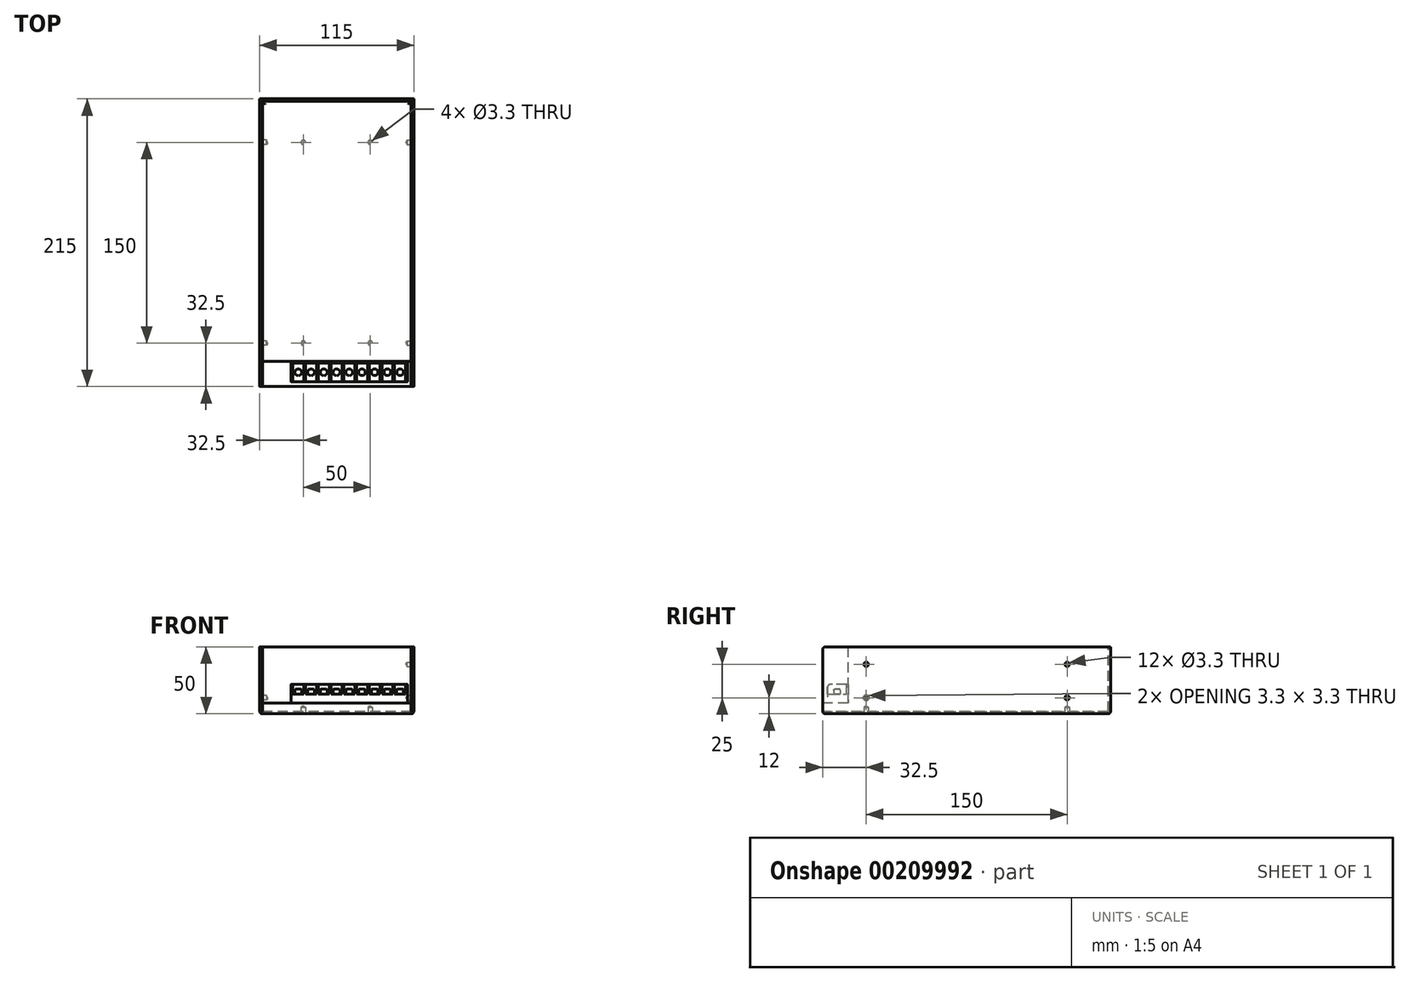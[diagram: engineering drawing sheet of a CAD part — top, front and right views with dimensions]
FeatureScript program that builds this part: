
annotation { "Feature Type Name" : "Feature", "Feature Type Description" : "" }
export const myFeature = defineFeature(function(context is Context, id is Id, definition is map)
    precondition{}
    {
        {
            var Q0;
            Q0=qCreatedBy(makeId("Front.planeOp"),FACE);
            var sketch = newSketch(context, id + "F0", { "sketchPlane" : qUnion([Q0])});
            skLineSegment(sketch, "E0.bottom", {"start": v(-57.5, 25) * mm, "end": v(0, 25) * mm});
            skLineSegment(sketch, "E0.top", {"start": v(-57.5, -25) * mm, "end": v(0, -25) * mm});
            skLineSegment(sketch, "E0.left", {"start": v(-57.5, 25) * mm, "end": v(-57.5, -25) * mm});
            skLineSegment(sketch, "E0.right", {"start": v(0, 25) * mm, "end": v(0, -25) * mm});
            skLineSegment(sketch, "E1", {"start": v(0, 0) * mm, "end": v(0, 48.13) * mm, "construction": true});
            skLineSegment(sketch, "E2", {"start": v(0, 0) * mm, "end": v(-98.9, 0) * mm, "construction": true});
            skPoint(sketch, "E2.endSnap0", {"position": v(0, 0) * mm});
            skSolve(sketch);
        }
        {
            var Q0;
            Q0=makeQuery(id+"F0.imprint","IMPRINT",FACE,{"disambiguationData":[TD([[makeQuery(id+"F0.imprint","IMPRINT",EDGE,{"derivedFrom":sQuery(id+"F0.wireOp",EDGE,"E0.bottom")}),-1.0]])]});
            extrude(context, id + "F1", {"entities" : qUnion([Q0]), "endBound" : BoundingType.SYMMETRIC, "depth" : 215 * mm});
        }
        {
            var Q0;
            Q0=makeQuery(id+"F1.opExtrude","SWEPT_FACE",FACE,{"disambiguationData":[OSD([sQuery(id+"F0.wireOp",EDGE,"E0.bottom")])]});
            var sketch = newSketch(context, id + "F2", { "sketchPlane" : qUnion([Q0])});
            skLineSegment(sketch, "E3.bottom", {"start": v(0, -107.5) * mm, "end": v(-55.8, -107.5) * mm});
            skLineSegment(sketch, "E3.top", {"start": v(0, -88.5) * mm, "end": v(-55.8, -88.5) * mm});
            skLineSegment(sketch, "E3.left", {"start": v(0, -107.5) * mm, "end": v(0, -88.5) * mm});
            skLineSegment(sketch, "E3.right", {"start": v(-55.8, -107.5) * mm, "end": v(-55.8, -88.5) * mm});
            skSolve(sketch);
        }
        {
            var Q0;
            Q0=makeQuery(id+"F2.imprint","IMPRINT",FACE,{"disambiguationData":[TD([[makeQuery(id+"F2.imprint","IMPRINT",EDGE,{"derivedFrom":sQuery(id+"F2.wireOp",EDGE,"E3.bottom")}),1.0]])]});
            extrude(context, id + "F3", {"entities" : qUnion([Q0]), "operationType" : NewBodyOperationType.REMOVE, "oppositeDirection" : true, "depth" : 42 * mm});
        }
        {
            var Q0;
            Q0=makeQuery(id+"F1.opExtrude","SWEPT_FACE",FACE,{"disambiguationData":[OSD([sQuery(id+"F0.wireOp",EDGE,"E0.bottom")])]});
            var sketch = newSketch(context, id + "F4", { "sketchPlane" : qUnion([Q0])});
            skLineSegment(sketch, "E4", {"start": v(-55.8, -107.5) * mm, "end": v(-55.8, 107.5) * mm});
            skLineSegment(sketch, "E5", {"start": v(-55.8, 107.5) * mm, "end": v(-55.5, 107.5) * mm});
            skLineSegment(sketch, "E6", {"start": v(-55.5, 107.5) * mm, "end": v(-55.5, 105.8) * mm});
            skLineSegment(sketch, "E7", {"start": v(-55.5, 105.8) * mm, "end": v(0, 105.8) * mm});
            skLineSegment(sketch, "E8", {"start": v(0, 105.8) * mm, "end": v(0, 105.5) * mm});
            skLineSegment(sketch, "E9", {"start": v(0, 105.5) * mm, "end": v(-55.5, 105.5) * mm});
            skLineSegment(sketch, "E10", {"start": v(-55.5, 105.5) * mm, "end": v(-55.5, -107.5) * mm});
            skLineSegment(sketch, "E11", {"start": v(-55.5, -107.5) * mm, "end": v(-55.8, -107.5) * mm});
            skSolve(sketch);
        }
        {
            var Q0;
            {var subQ1=sQuery(id+"F4.wireOp",EDGE,"E5");Q0=makeQuery(id+"F4.imprint","IMPRINT",FACE,{"disambiguationData":[TD([[makeQuery(id+"F4.imprint","IMPRINT",EDGE,{"derivedFrom":subQ1}),-1.0]])]});}
            var Q1;
            {var subQ0=sQuery(id+"F4.wireOp",EDGE,"E11");Q1=makeQuery(id+"F4.imprint","IMPRINT",FACE,{"disambiguationData":[TD([[makeQuery(id+"F4.imprint","IMPRINT",EDGE,{"derivedFrom":subQ0}),-1.0]])]});}
            extrude(context, id + "F5", {"entities" : qUnion([Q0, Q1]), "operationType" : NewBodyOperationType.REMOVE, "oppositeDirection" : true, "depth" : 48.3 * mm});
        }
        {
            var Q0;
            Q0=makeQuery(id+"F3.boolean.opBoolean","COPY",EDGE,{"derivedFrom":makeQuery(id+"F3.opExtrude","CAP_EDGE",EDGE,{"disambiguationData":[OSD([sQuery(id+"F2.wireOp",EDGE,"E3.top")])],"isStart":true})});
            var Q1;
            Q1=makeQuery(id+"F1.opExtrude","CAP_EDGE",EDGE,{"disambiguationData":[OSD([sQuery(id+"F0.wireOp",EDGE,"E0.top")])],"isStart":false});
            var Q2;
            Q2=makeQuery(id+"F1.opExtrude","SWEPT_EDGE",EDGE,{"disambiguationData":[OSD([sQuery(id+"F0.wireOp",EDGE,"E0.top"),sQuery(id+"F0.wireOp",EDGE,"E0.left")])]});
            var Q3;
            Q3=makeQuery(id+"F1.opExtrude","CAP_EDGE",EDGE,{"disambiguationData":[OSD([sQuery(id+"F0.wireOp",EDGE,"E0.top")])],"isStart":true});
            var Q4;
            Q4=makeQuery(id+"F1.opExtrude","CAP_EDGE",EDGE,{"disambiguationData":[OSD([sQuery(id+"F0.wireOp",EDGE,"E0.bottom")])],"isStart":false});
            var Q5;
            {var subQ0=sQuery(id+"F0.wireOp",EDGE,"E0.bottom");var subQ1=sQuery(id+"F0.wireOp",EDGE,"E0.left");Q5=makeQuery(id+"F5.boolean.opBoolean","SPLIT",EDGE,{"disambiguationData":[TD([makeQuery(id+"F1.opExtrude","SWEPT_FACE",FACE,{"disambiguationData":[OSD([subQ1])]})])],"derivedFrom":makeQuery(id+"F1.opExtrude","CAP_EDGE",EDGE,{"disambiguationData":[OSD([subQ0])],"isStart":true})});}
            var Q6;
            Q6=makeQuery(id+"F5.boolean.opBoolean","COPY",EDGE,{"derivedFrom":makeQuery(id+"F5.opExtrude","CAP_EDGE",EDGE,{"disambiguationData":[OSD([sQuery(id+"F4.wireOp",EDGE,"E6")])],"isStart":true})});
            var Q7;
            Q7=makeQuery(id+"F5.boolean.opBoolean","COPY",EDGE,{"derivedFrom":makeQuery(id+"F5.opExtrude","CAP_EDGE",EDGE,{"disambiguationData":[OSD([sQuery(id+"F4.wireOp",EDGE,"E9")])],"isStart":true})});
            var Q8;
            Q8=makeQuery(id+"F5.boolean.opBoolean","COPY",EDGE,{"derivedFrom":makeQuery(id+"F5.opExtrude","CAP_EDGE",EDGE,{"disambiguationData":[OSD([sQuery(id+"F4.wireOp",EDGE,"E10")])],"isStart":true})});
            fillet(context, id + "F6", {"entities" : qUnion([Q0, Q1, Q2, Q3, Q4, Q5, Q6, Q7, Q8]), "radius" : 2 * mm, "tangentPropagation" : true, "allowEdgeOverflow" : false});
        }
        {
            var Q0;
            Q0=makeQuery(id+"F1.opExtrude","SWEPT_BODY",BODY,{"disambiguationData":[OSD([sQuery(id+"F0.wireOp",EDGE,"E0.bottom"),sQuery(id+"F0.wireOp",EDGE,"E0.top"),sQuery(id+"F0.wireOp",EDGE,"E0.left"),sQuery(id+"F0.wireOp",EDGE,"E0.right")])]});
            var Q1;
            Q1=qCreatedBy(makeId("Right.planeOp"),FACE);
            mirror(context, id + "F7", {"operationType" : NewBodyOperationType.ADD, "entities" : qUnion([Q0]), "mirrorPlane" : qUnion([Q1])});
        }
        {
            var Q0;
            {var subQ0=makeQuery(id+"F3.boolean.opBoolean","COPY",FACE,{"derivedFrom":makeQuery(id+"F3.opExtrude","CAP_FACE",FACE,{"disambiguationData":[OSD([sQuery(id+"F2.wireOp",EDGE,"E3.bottom"),sQuery(id+"F2.wireOp",EDGE,"E3.top"),sQuery(id+"F2.wireOp",EDGE,"E3.left"),sQuery(id+"F2.wireOp",EDGE,"E3.right")])],"isStart":false})});Q0=makeQuery(id+"F7.boolean.opBoolean","MERGE",FACE,{"derivedFrom":[subQ0,makeQuery(id+"F7.opPattern","COPY",FACE,{"derivedFrom":subQ0,"instanceName":"1"})]});}
            var sketch = newSketch(context, id + "F8", { "sketchPlane" : qUnion([Q0])});
            skLineSegment(sketch, "E12.bottom", {"start": v(-34.2, -88.5) * mm, "end": v(52.8, -88.5) * mm});
            skLineSegment(sketch, "E12.top", {"start": v(-34.2, -103.8) * mm, "end": v(52.8, -103.8) * mm});
            skLineSegment(sketch, "E12.left", {"start": v(-34.2, -88.5) * mm, "end": v(-34.2, -103.8) * mm});
            skLineSegment(sketch, "E12.right", {"start": v(52.8, -88.5) * mm, "end": v(52.8, -103.8) * mm});
            skSolve(sketch);
        }
        {
            var Q0;
            Q0=makeQuery(id+"F8.imprint","IMPRINT",FACE,{"disambiguationData":[TD([[makeQuery(id+"F8.imprint","IMPRINT",EDGE,{"derivedFrom":sQuery(id+"F8.wireOp",EDGE,"E12.bottom")}),1.0]])]});
            extrude(context, id + "F9", {"entities" : qUnion([Q0]), "depth" : 14 * mm});
        }
        {
            var Q0;
            Q0=makeQuery(id+"F9.opExtrude","CAP_FACE",FACE,{"disambiguationData":[OSD([sQuery(id+"F8.wireOp",EDGE,"E12.bottom"),sQuery(id+"F8.wireOp",EDGE,"E12.top"),sQuery(id+"F8.wireOp",EDGE,"E12.left"),sQuery(id+"F8.wireOp",EDGE,"E12.right")])],"isStart":false});
            var sketch = newSketch(context, id + "F10", { "sketchPlane" : qUnion([Q0])});
            skLineSegment(sketch, "E13", {"start": v(-32.8, -103.8) * mm, "end": v(-32.8, -89.8) * mm});
            skLineSegment(sketch, "E14", {"start": v(-32.8, -89.8) * mm, "end": v(-24.6, -89.8) * mm});
            skLineSegment(sketch, "E15", {"start": v(-24.6, -89.8) * mm, "end": v(-24.6, -103.8) * mm});
            skLineSegment(sketch, "E16", {"start": v(-24.6, -103.8) * mm, "end": v(-32.8, -103.8) * mm});
            skLineSegment(sketch, "E17.1.0.0", {"start": v(-23.3, -103.8) * mm, "end": v(-23.3, -89.8) * mm});
            skLineSegment(sketch, "E17.1.0.1", {"start": v(-15.1, -103.8) * mm, "end": v(-23.3, -103.8) * mm});
            skLineSegment(sketch, "E17.1.0.2", {"start": v(-15.1, -89.8) * mm, "end": v(-15.1, -103.8) * mm});
            skLineSegment(sketch, "E17.1.0.3", {"start": v(-23.3, -89.8) * mm, "end": v(-15.1, -89.8) * mm});
            skLineSegment(sketch, "E17.2.0.0", {"start": v(-13.8, -103.8) * mm, "end": v(-13.8, -89.8) * mm});
            skLineSegment(sketch, "E17.2.0.1", {"start": v(-5.6, -103.8) * mm, "end": v(-13.8, -103.8) * mm});
            skLineSegment(sketch, "E17.2.0.2", {"start": v(-5.6, -89.8) * mm, "end": v(-5.6, -103.8) * mm});
            skLineSegment(sketch, "E17.2.0.3", {"start": v(-13.8, -89.8) * mm, "end": v(-5.6, -89.8) * mm});
            skLineSegment(sketch, "E17.3.0.0", {"start": v(-4.3, -103.8) * mm, "end": v(-4.3, -89.8) * mm});
            skLineSegment(sketch, "E17.3.0.1", {"start": v(3.9, -103.8) * mm, "end": v(-4.3, -103.8) * mm});
            skLineSegment(sketch, "E17.3.0.2", {"start": v(3.9, -89.8) * mm, "end": v(3.9, -103.8) * mm});
            skLineSegment(sketch, "E17.3.0.3", {"start": v(-4.3, -89.8) * mm, "end": v(3.9, -89.8) * mm});
            skLineSegment(sketch, "E17.4.0.0", {"start": v(5.2, -103.8) * mm, "end": v(5.2, -89.8) * mm});
            skLineSegment(sketch, "E17.4.0.1", {"start": v(13.4, -103.8) * mm, "end": v(5.2, -103.8) * mm});
            skLineSegment(sketch, "E17.4.0.2", {"start": v(13.4, -89.8) * mm, "end": v(13.4, -103.8) * mm});
            skLineSegment(sketch, "E17.4.0.3", {"start": v(5.2, -89.8) * mm, "end": v(13.4, -89.8) * mm});
            skLineSegment(sketch, "E17.5.0.0", {"start": v(14.7, -103.8) * mm, "end": v(14.7, -89.8) * mm});
            skLineSegment(sketch, "E17.5.0.1", {"start": v(22.9, -103.8) * mm, "end": v(14.7, -103.8) * mm});
            skLineSegment(sketch, "E17.5.0.2", {"start": v(22.9, -89.8) * mm, "end": v(22.9, -103.8) * mm});
            skLineSegment(sketch, "E17.5.0.3", {"start": v(14.7, -89.8) * mm, "end": v(22.9, -89.8) * mm});
            skLineSegment(sketch, "E17.6.0.0", {"start": v(24.2, -103.8) * mm, "end": v(24.2, -89.8) * mm});
            skLineSegment(sketch, "E17.6.0.1", {"start": v(32.4, -103.8) * mm, "end": v(24.2, -103.8) * mm});
            skLineSegment(sketch, "E17.6.0.2", {"start": v(32.4, -89.8) * mm, "end": v(32.4, -103.8) * mm});
            skLineSegment(sketch, "E17.6.0.3", {"start": v(24.2, -89.8) * mm, "end": v(32.4, -89.8) * mm});
            skLineSegment(sketch, "E17.7.0.0", {"start": v(33.7, -103.8) * mm, "end": v(33.7, -89.8) * mm});
            skLineSegment(sketch, "E17.7.0.1", {"start": v(41.9, -103.8) * mm, "end": v(33.7, -103.8) * mm});
            skLineSegment(sketch, "E17.7.0.2", {"start": v(41.9, -89.8) * mm, "end": v(41.9, -103.8) * mm});
            skLineSegment(sketch, "E17.7.0.3", {"start": v(33.7, -89.8) * mm, "end": v(41.9, -89.8) * mm});
            skLineSegment(sketch, "E17.8.0.0", {"start": v(43.2, -103.8) * mm, "end": v(43.2, -89.8) * mm});
            skLineSegment(sketch, "E17.8.0.1", {"start": v(51.4, -103.8) * mm, "end": v(43.2, -103.8) * mm});
            skLineSegment(sketch, "E17.8.0.2", {"start": v(51.4, -89.8) * mm, "end": v(51.4, -103.8) * mm});
            skLineSegment(sketch, "E17.8.0.3", {"start": v(43.2, -89.8) * mm, "end": v(51.4, -89.8) * mm});
            skLineSegment(sketch, "E17.direction1", {"start": v(-32.8, -103.8) * mm, "end": v(-23.3, -103.8) * mm, "construction": true});
            skSolve(sketch);
        }
        {
            var Q0;
            Q0=makeQuery(id+"F10.imprint","IMPRINT",FACE,{"disambiguationData":[TD([[makeQuery(id+"F10.imprint","IMPRINT",EDGE,{"derivedFrom":sQuery(id+"F10.wireOp",EDGE,"E13")}),-1.0]])]});
            var Q1;
            Q1=makeQuery(id+"F10.imprint","IMPRINT",FACE,{"disambiguationData":[TD([[makeQuery(id+"F10.imprint","IMPRINT",EDGE,{"derivedFrom":sQuery(id+"F10.wireOp",EDGE,"E17.1.0.0")}),-1.0]])]});
            var Q2;
            Q2=makeQuery(id+"F10.imprint","IMPRINT",FACE,{"disambiguationData":[TD([[makeQuery(id+"F10.imprint","IMPRINT",EDGE,{"derivedFrom":sQuery(id+"F10.wireOp",EDGE,"E17.2.0.0")}),-1.0]])]});
            var Q3;
            Q3=makeQuery(id+"F10.imprint","IMPRINT",FACE,{"disambiguationData":[TD([[makeQuery(id+"F10.imprint","IMPRINT",EDGE,{"derivedFrom":sQuery(id+"F10.wireOp",EDGE,"E17.3.0.0")}),-1.0]])]});
            var Q4;
            Q4=makeQuery(id+"F10.imprint","IMPRINT",FACE,{"disambiguationData":[TD([[makeQuery(id+"F10.imprint","IMPRINT",EDGE,{"derivedFrom":sQuery(id+"F10.wireOp",EDGE,"E17.4.0.0")}),-1.0]])]});
            var Q5;
            Q5=makeQuery(id+"F10.imprint","IMPRINT",FACE,{"disambiguationData":[TD([[makeQuery(id+"F10.imprint","IMPRINT",EDGE,{"derivedFrom":sQuery(id+"F10.wireOp",EDGE,"E17.5.0.0")}),-1.0]])]});
            var Q6;
            Q6=makeQuery(id+"F10.imprint","IMPRINT",FACE,{"disambiguationData":[TD([[makeQuery(id+"F10.imprint","IMPRINT",EDGE,{"derivedFrom":sQuery(id+"F10.wireOp",EDGE,"E17.6.0.0")}),-1.0]])]});
            var Q7;
            Q7=makeQuery(id+"F10.imprint","IMPRINT",FACE,{"disambiguationData":[TD([[makeQuery(id+"F10.imprint","IMPRINT",EDGE,{"derivedFrom":sQuery(id+"F10.wireOp",EDGE,"E17.7.0.0")}),-1.0]])]});
            var Q8;
            Q8=makeQuery(id+"F10.imprint","IMPRINT",FACE,{"disambiguationData":[TD([[makeQuery(id+"F10.imprint","IMPRINT",EDGE,{"derivedFrom":sQuery(id+"F10.wireOp",EDGE,"E17.8.0.0")}),-1.0]])]});
            extrude(context, id + "F11", {"entities" : qUnion([Q0, Q1, Q2, Q3, Q4, Q5, Q6, Q7, Q8]), "operationType" : NewBodyOperationType.REMOVE, "oppositeDirection" : true, "depth" : 7.4 * mm});
        }
        {
            var Q0;
            {var subQ0=sQuery(id+"F8.wireOp",EDGE,"E12.left");var subQ1=sQuery(id+"F8.wireOp",EDGE,"E12.top");Q0=makeQuery(id+"F11.boolean.opBoolean","SPLIT",EDGE,{"disambiguationData":[TD([makeQuery(id+"F9.opExtrude","SWEPT_FACE",FACE,{"disambiguationData":[OSD([subQ0])]})])],"derivedFrom":makeQuery(id+"F9.opExtrude","CAP_EDGE",EDGE,{"disambiguationData":[OSD([subQ1])],"isStart":false})});}
            var Q1;
            {var subQ0=sQuery(id+"F8.wireOp",EDGE,"E12.top");Q1=makeQuery(id+"F11.boolean.opBoolean","SPLIT",EDGE,{"disambiguationData":[TD([makeQuery(id+"F11.opExtrude","SWEPT_FACE",FACE,{"disambiguationData":[OSD([sQuery(id+"F10.wireOp",EDGE,"E15")])]})])],"derivedFrom":makeQuery(id+"F9.opExtrude","CAP_EDGE",EDGE,{"disambiguationData":[OSD([subQ0])],"isStart":false})});}
            var Q2;
            {var subQ0=sQuery(id+"F8.wireOp",EDGE,"E12.top");Q2=makeQuery(id+"F11.boolean.opBoolean","SPLIT",EDGE,{"disambiguationData":[TD([makeQuery(id+"F11.opExtrude","SWEPT_FACE",FACE,{"disambiguationData":[OSD([sQuery(id+"F10.wireOp",EDGE,"E17.1.0.2")])]})])],"derivedFrom":makeQuery(id+"F9.opExtrude","CAP_EDGE",EDGE,{"disambiguationData":[OSD([subQ0])],"isStart":false})});}
            var Q3;
            {var subQ0=sQuery(id+"F8.wireOp",EDGE,"E12.top");Q3=makeQuery(id+"F11.boolean.opBoolean","SPLIT",EDGE,{"disambiguationData":[TD([makeQuery(id+"F11.opExtrude","SWEPT_FACE",FACE,{"disambiguationData":[OSD([sQuery(id+"F10.wireOp",EDGE,"E17.2.0.2")])]})])],"derivedFrom":makeQuery(id+"F9.opExtrude","CAP_EDGE",EDGE,{"disambiguationData":[OSD([subQ0])],"isStart":false})});}
            var Q4;
            {var subQ0=sQuery(id+"F8.wireOp",EDGE,"E12.top");Q4=makeQuery(id+"F11.boolean.opBoolean","SPLIT",EDGE,{"disambiguationData":[TD([makeQuery(id+"F11.opExtrude","SWEPT_FACE",FACE,{"disambiguationData":[OSD([sQuery(id+"F10.wireOp",EDGE,"E17.3.0.2")])]})])],"derivedFrom":makeQuery(id+"F9.opExtrude","CAP_EDGE",EDGE,{"disambiguationData":[OSD([subQ0])],"isStart":false})});}
            var Q5;
            {var subQ0=sQuery(id+"F8.wireOp",EDGE,"E12.top");Q5=makeQuery(id+"F11.boolean.opBoolean","SPLIT",EDGE,{"disambiguationData":[TD([makeQuery(id+"F11.opExtrude","SWEPT_FACE",FACE,{"disambiguationData":[OSD([sQuery(id+"F10.wireOp",EDGE,"E17.4.0.2")])]})])],"derivedFrom":makeQuery(id+"F9.opExtrude","CAP_EDGE",EDGE,{"disambiguationData":[OSD([subQ0])],"isStart":false})});}
            var Q6;
            {var subQ0=sQuery(id+"F8.wireOp",EDGE,"E12.top");Q6=makeQuery(id+"F11.boolean.opBoolean","SPLIT",EDGE,{"disambiguationData":[TD([makeQuery(id+"F11.opExtrude","SWEPT_FACE",FACE,{"disambiguationData":[OSD([sQuery(id+"F10.wireOp",EDGE,"E17.5.0.2")])]})])],"derivedFrom":makeQuery(id+"F9.opExtrude","CAP_EDGE",EDGE,{"disambiguationData":[OSD([subQ0])],"isStart":false})});}
            var Q7;
            {var subQ0=sQuery(id+"F8.wireOp",EDGE,"E12.top");Q7=makeQuery(id+"F11.boolean.opBoolean","SPLIT",EDGE,{"disambiguationData":[TD([makeQuery(id+"F11.opExtrude","SWEPT_FACE",FACE,{"disambiguationData":[OSD([sQuery(id+"F10.wireOp",EDGE,"E17.6.0.2")])]})])],"derivedFrom":makeQuery(id+"F9.opExtrude","CAP_EDGE",EDGE,{"disambiguationData":[OSD([subQ0])],"isStart":false})});}
            var Q8;
            {var subQ0=sQuery(id+"F8.wireOp",EDGE,"E12.top");Q8=makeQuery(id+"F11.boolean.opBoolean","SPLIT",EDGE,{"disambiguationData":[TD([makeQuery(id+"F11.opExtrude","SWEPT_FACE",FACE,{"disambiguationData":[OSD([sQuery(id+"F10.wireOp",EDGE,"E17.7.0.2")])]})])],"derivedFrom":makeQuery(id+"F9.opExtrude","CAP_EDGE",EDGE,{"disambiguationData":[OSD([subQ0])],"isStart":false})});}
            var Q9;
            {var subQ0=sQuery(id+"F8.wireOp",EDGE,"E12.right");var subQ1=sQuery(id+"F8.wireOp",EDGE,"E12.top");Q9=makeQuery(id+"F11.boolean.opBoolean","SPLIT",EDGE,{"disambiguationData":[TD([makeQuery(id+"F9.opExtrude","SWEPT_FACE",FACE,{"disambiguationData":[OSD([subQ0])]})])],"derivedFrom":makeQuery(id+"F9.opExtrude","CAP_EDGE",EDGE,{"disambiguationData":[OSD([subQ1])],"isStart":false})});}
            fillet(context, id + "F12", {"entities" : qUnion([Q0, Q1, Q2, Q3, Q4, Q5, Q6, Q7, Q8, Q9]), "radius" : 2 * mm, "tangentPropagation" : true, "allowEdgeOverflow" : false});
        }
        {
            var Q0;
            Q0=makeQuery(id+"F11.boolean.opBoolean","COPY",FACE,{"derivedFrom":makeQuery(id+"F11.opExtrude","CAP_FACE",FACE,{"disambiguationData":[OSD([sQuery(id+"F10.wireOp",EDGE,"E13"),sQuery(id+"F10.wireOp",EDGE,"E14"),sQuery(id+"F10.wireOp",EDGE,"E15"),sQuery(id+"F10.wireOp",EDGE,"E16")])],"isStart":false})});
            var sketch = newSketch(context, id + "F13", { "sketchPlane" : qUnion([Q0])});
            skLineSegment(sketch, "E18", {"start": v(-32.8, -89.8) * mm, "end": v(-24.6, -103.8) * mm, "construction": true});
            skCircle(sketch, "E19", {"center": v(-28.7, -96.8) * mm, "radius": 2.5 * mm});
            skCircle(sketch, "E20.1.0.0", {"center": v(-19.2, -96.8) * mm, "radius": 2.5 * mm});
            skCircle(sketch, "E20.2.0.0", {"center": v(-9.7, -96.8) * mm, "radius": 2.5 * mm});
            skCircle(sketch, "E20.3.0.0", {"center": v(-0.2, -96.8) * mm, "radius": 2.5 * mm});
            skCircle(sketch, "E20.4.0.0", {"center": v(9.3, -96.8) * mm, "radius": 2.5 * mm});
            skCircle(sketch, "E20.5.0.0", {"center": v(18.8, -96.8) * mm, "radius": 2.5 * mm});
            skCircle(sketch, "E20.6.0.0", {"center": v(28.3, -96.8) * mm, "radius": 2.5 * mm});
            skCircle(sketch, "E20.7.0.0", {"center": v(37.8, -96.8) * mm, "radius": 2.5 * mm});
            skCircle(sketch, "E20.8.0.0", {"center": v(47.3, -96.8) * mm, "radius": 2.5 * mm});
            skLineSegment(sketch, "E20.direction1", {"start": v(-28.7, -96.8) * mm, "end": v(-19.2, -96.8) * mm, "construction": true});
            skSolve(sketch);
        }
        {
            var Q0;
            Q0=makeQuery(id+"F13.imprint","IMPRINT",FACE,{"disambiguationData":[TD([[makeQuery(id+"F13.imprint","IMPRINT",EDGE,{"derivedFrom":sQuery(id+"F13.wireOp",EDGE,"E19")}),1.0]])]});
            var Q1;
            Q1=makeQuery(id+"F13.imprint","IMPRINT",FACE,{"disambiguationData":[TD([[makeQuery(id+"F13.imprint","IMPRINT",EDGE,{"derivedFrom":sQuery(id+"F13.wireOp",EDGE,"E20.1.0.0")}),1.0]])]});
            var Q2;
            Q2=makeQuery(id+"F13.imprint","IMPRINT",FACE,{"disambiguationData":[TD([[makeQuery(id+"F13.imprint","IMPRINT",EDGE,{"derivedFrom":sQuery(id+"F13.wireOp",EDGE,"E20.2.0.0")}),1.0]])]});
            var Q3;
            Q3=makeQuery(id+"F13.imprint","IMPRINT",FACE,{"disambiguationData":[TD([[makeQuery(id+"F13.imprint","IMPRINT",EDGE,{"derivedFrom":sQuery(id+"F13.wireOp",EDGE,"E20.3.0.0")}),1.0]])]});
            var Q4;
            Q4=makeQuery(id+"F13.imprint","IMPRINT",FACE,{"disambiguationData":[TD([[makeQuery(id+"F13.imprint","IMPRINT",EDGE,{"derivedFrom":sQuery(id+"F13.wireOp",EDGE,"E20.4.0.0")}),1.0]])]});
            var Q5;
            Q5=makeQuery(id+"F13.imprint","IMPRINT",FACE,{"disambiguationData":[TD([[makeQuery(id+"F13.imprint","IMPRINT",EDGE,{"derivedFrom":sQuery(id+"F13.wireOp",EDGE,"E20.5.0.0")}),1.0]])]});
            var Q6;
            Q6=makeQuery(id+"F13.imprint","IMPRINT",FACE,{"disambiguationData":[TD([[makeQuery(id+"F13.imprint","IMPRINT",EDGE,{"derivedFrom":sQuery(id+"F13.wireOp",EDGE,"E20.6.0.0")}),1.0]])]});
            var Q7;
            Q7=makeQuery(id+"F13.imprint","IMPRINT",FACE,{"disambiguationData":[TD([[makeQuery(id+"F13.imprint","IMPRINT",EDGE,{"derivedFrom":sQuery(id+"F13.wireOp",EDGE,"E20.7.0.0")}),1.0]])]});
            var Q8;
            Q8=makeQuery(id+"F13.imprint","IMPRINT",FACE,{"disambiguationData":[TD([[makeQuery(id+"F13.imprint","IMPRINT",EDGE,{"derivedFrom":sQuery(id+"F13.wireOp",EDGE,"E20.8.0.0")}),1.0]])]});
            var Q9;
            Q9=sQuery(id+"F13.wireOp",EDGE,"E19");
            extrude(context, id + "F14", {"entities" : qUnion([Q0, Q1, Q2, Q3, Q4, Q5, Q6, Q7, Q8]), "operationType" : NewBodyOperationType.ADD, "surfaceEntities" : qUnion([Q9]), "depth" : 4 * mm});
        }
        {
            var Q0;
            Q0=makeQuery(id+"F14.opExtrude","CAP_EDGE",EDGE,{"disambiguationData":[OSD([sQuery(id+"F13.wireOp",EDGE,"E19")])],"isStart":false});
            var Q1;
            Q1=makeQuery(id+"F14.opExtrude","CAP_EDGE",EDGE,{"disambiguationData":[OSD([sQuery(id+"F13.wireOp",EDGE,"E20.1.0.0")])],"isStart":false});
            var Q2;
            Q2=makeQuery(id+"F14.opExtrude","CAP_EDGE",EDGE,{"disambiguationData":[OSD([sQuery(id+"F13.wireOp",EDGE,"E20.2.0.0")])],"isStart":false});
            var Q3;
            Q3=makeQuery(id+"F14.opExtrude","CAP_EDGE",EDGE,{"disambiguationData":[OSD([sQuery(id+"F13.wireOp",EDGE,"E20.3.0.0")])],"isStart":false});
            var Q4;
            Q4=makeQuery(id+"F14.opExtrude","CAP_EDGE",EDGE,{"disambiguationData":[OSD([sQuery(id+"F13.wireOp",EDGE,"E20.4.0.0")])],"isStart":false});
            var Q5;
            Q5=makeQuery(id+"F14.opExtrude","CAP_EDGE",EDGE,{"disambiguationData":[OSD([sQuery(id+"F13.wireOp",EDGE,"E20.5.0.0")])],"isStart":false});
            var Q6;
            Q6=makeQuery(id+"F14.opExtrude","CAP_EDGE",EDGE,{"disambiguationData":[OSD([sQuery(id+"F13.wireOp",EDGE,"E20.6.0.0")])],"isStart":false});
            var Q7;
            Q7=makeQuery(id+"F14.opExtrude","CAP_EDGE",EDGE,{"disambiguationData":[OSD([sQuery(id+"F13.wireOp",EDGE,"E20.7.0.0")])],"isStart":false});
            var Q8;
            Q8=makeQuery(id+"F14.opExtrude","CAP_EDGE",EDGE,{"disambiguationData":[OSD([sQuery(id+"F13.wireOp",EDGE,"E20.8.0.0")])],"isStart":false});
            fillet(context, id + "F15", {"entities" : qUnion([Q0, Q1, Q2, Q3, Q4, Q5, Q6, Q7, Q8]), "radius" : 1 * mm, "tangentPropagation" : true, "allowEdgeOverflow" : false});
        }
        {
            var Q0;
            Q0=makeQuery(id+"F1.opExtrude","SWEPT_FACE",FACE,{"disambiguationData":[OSD([sQuery(id+"F0.wireOp",EDGE,"E0.left")])]});
            var sketch = newSketch(context, id + "F16", { "sketchPlane" : qUnion([Q0])});
            skLineSegment(sketch, "E21", {"start": v(-75, -13) * mm, "end": v(75, -13) * mm});
            skLineSegment(sketch, "E22", {"start": v(0, 0) * mm, "end": v(0, -13) * mm});
            skSolve(sketch);
        }
        {
            var Q0;
            Q0=makeQuery(id+"F7.opPattern","COPY",FACE,{"derivedFrom":makeQuery(id+"F1.opExtrude","SWEPT_FACE",FACE,{"disambiguationData":[OSD([sQuery(id+"F0.wireOp",EDGE,"E0.left")])]}),"instanceName":"1"});
            var sketch = newSketch(context, id + "F17", { "sketchPlane" : qUnion([Q0])});
            skPoint(sketch, "E23.0", {"position": v(-75, -13) * mm});
            skPoint(sketch, "E23.1", {"position": v(75, -13) * mm});
            skPoint(sketch, "E24", {"position": v(-75, 12) * mm});
            skPoint(sketch, "E25", {"position": v(75, 12) * mm});
            skSolve(sketch);
        }
        {
            var Q0;
            {var subQ0=makeQuery(id+"F1.opExtrude","SWEPT_FACE",FACE,{"disambiguationData":[OSD([sQuery(id+"F0.wireOp",EDGE,"E0.top")])]});Q0=makeQuery(id+"F7.boolean.opBoolean","MERGE",FACE,{"derivedFrom":[subQ0,makeQuery(id+"F7.opPattern","COPY",FACE,{"derivedFrom":subQ0,"instanceName":"1"})]});}
            var sketch = newSketch(context, id + "F18", { "sketchPlane" : qUnion([Q0])});
            skLineSegment(sketch, "E26", {"start": v(-21.97, 0) * mm, "end": v(0, 0) * mm, "construction": true});
            skLineSegment(sketch, "E27", {"start": v(0, 0) * mm, "end": v(0, 32.91) * mm, "construction": true});
            skPoint(sketch, "E28", {"position": v(-25, 75) * mm});
            skPoint(sketch, "E29.MirrorP", {"position": v(-25, -75) * mm});
            skPoint(sketch, "E30.MirrorP", {"position": v(25, -75) * mm});
            skPoint(sketch, "E31.MirrorP", {"position": v(25, 75) * mm});
            skSolve(sketch);
        }
        {
            var Q0;
            Q0=sQuery(id+"F16.wireOp",VERTEX,"E21.start");
            var Q1;
            Q1=sQuery(id+"F16.wireOp",VERTEX,"E21.end");
            var Q2;
            Q2=sQuery(id+"F18.wireOp",VERTEX,"E29.MirrorP");
            var Q3;
            Q3=sQuery(id+"F18.wireOp",VERTEX,"E28");
            var Q4;
            Q4=sQuery(id+"F18.wireOp",VERTEX,"E30.MirrorP");
            var Q5;
            Q5=sQuery(id+"F18.wireOp",VERTEX,"E31.MirrorP");
            var Q6;
            Q6=sQuery(id+"F17.wireOp",VERTEX,"E23.0");
            var Q7;
            Q7=sQuery(id+"F17.wireOp",VERTEX,"E24");
            var Q8;
            Q8=sQuery(id+"F17.wireOp",VERTEX,"E25");
            var Q9;
            Q9=sQuery(id+"F17.wireOp",VERTEX,"E23.1");
            var Q10;
            Q10=makeQuery(id+"F1.opExtrude","SWEPT_BODY",BODY,{"disambiguationData":[OSD([sQuery(id+"F0.wireOp",EDGE,"E0.bottom"),sQuery(id+"F0.wireOp",EDGE,"E0.top"),sQuery(id+"F0.wireOp",EDGE,"E0.left"),sQuery(id+"F0.wireOp",EDGE,"E0.right")])]});
            hole(context, id + "F19", {"style" : HoleStyle.SIMPLE, "endStyle" : HoleEndStyle.BLIND, "holeDiameter" : 3.3 * mm, "holeDepth" : 5 * mm, "locations" : qUnion([Q0, Q1, Q2, Q3, Q4, Q5, Q6, Q7, Q8, Q9]), "scope" : qUnion([Q10])});
        }
    });
